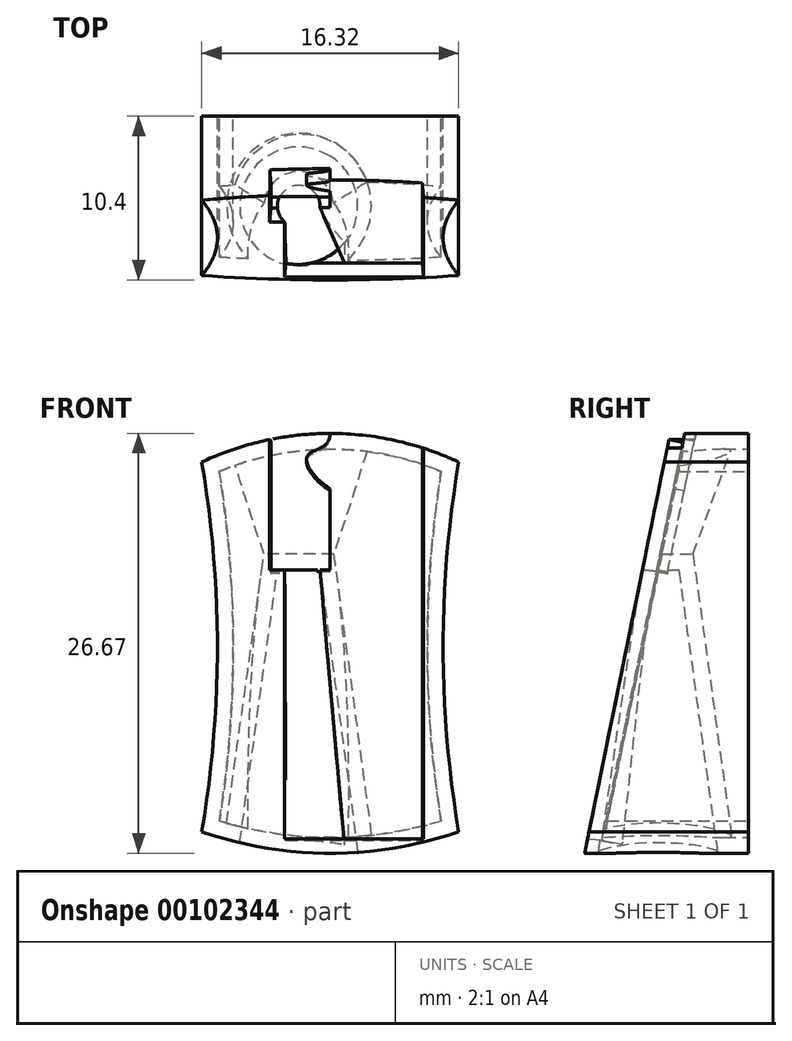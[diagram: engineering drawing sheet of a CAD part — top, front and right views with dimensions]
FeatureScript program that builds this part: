
annotation { "Feature Type Name" : "Feature", "Feature Type Description" : "" }
export const myFeature = defineFeature(function(context is Context, id is Id, definition is map)
    precondition{}
    {
        {
            var Q0;
            Q0=qCreatedBy(makeId("Front.planeOp"),FACE);
            var sketch = newSketch(context, id + "F0", { "sketchPlane" : qUnion([Q0])});
            skLineSegment(sketch, "E0", {"start": v(0, 26.67) * mm, "end": v(52.61, 26.67) * mm, "construction": true});
            skLineSegment(sketch, "E1", {"start": v(40.02, 26.67) * mm, "end": v(40.02, 0) * mm, "construction": true});
            skLineSegment(sketch, "E2", {"start": v(40.02, 13.34) * mm, "end": v(-78.87, 13.33) * mm, "construction": true});
            skLineSegment(sketch, "E3", {"start": v(0, 26.67) * mm, "end": v(0, 0) * mm});
            skPoint(sketch, "E4", {"position": v(-8.16, 1.37) * mm});
            skPoint(sketch, "E5", {"position": v(-8.16, 24.85) * mm});
            skArc(sketch, "E6.trimOffspring", {"start": v(-8.16, 1.37) * mm, "mid": v(-7.17, 13.1) * mm, "end": v(-8.16, 24.85) * mm});
            skArc(sketch, "E7.MirrorCS", {"start": v(8.16, 1.37) * mm, "mid": v(7.17, 13.1) * mm, "end": v(8.16, 24.85) * mm});
            skArc(sketch, "E8.trimOffspring", {"start": v(-8.16, 1.37) * mm, "mid": v(0, 0) * mm, "end": v(8.16, 1.37) * mm});
            skArc(sketch, "E9.trimOffspring", {"start": v(8.16, 24.85) * mm, "mid": v(0, 26.67) * mm, "end": v(-8.16, 24.85) * mm});
            skSolve(sketch);
        }
        {
            var Q0;
            Q0 = qSketchRegion(id + "F0", true);
            extrude(context, id + "F1", {"entities" : qUnion([Q0]), "endBound" : BoundingType.SYMMETRIC, "depth" : 11.45 * mm});
        }
        {
            var Q0;
            Q0=qCreatedBy(makeId("Right.planeOp"),FACE);
            cPlane(context, id + "F2", {"entities" : qUnion([Q0]), "cplaneType" : CPlaneType.OFFSET, "offset" : 2 * mm, "oppositeDirection" : true, "width" : 150 * mm, "height" : 150 * mm});
        }
        {
            var Q0;
            Q0=qCreatedBy(makeId("Top.planeOp"),FACE);
            cPlane(context, id + "F3", {"entities" : qUnion([Q0]), "cplaneType" : CPlaneType.OFFSET, "offset" : 18 * mm, "width" : 150 * mm, "height" : 150 * mm});
        }
        {
            var Q0;
            Q0=qCreatedBy(id+"F3.planeOp",FACE);
            var sketch = newSketch(context, id + "F4", { "sketchPlane" : qUnion([Q0])});
            skCircle(sketch, "E10", {"center": v(-2, 0) * mm, "radius": 1.34 * mm});
            skSolve(sketch);
        }
        {
            var Q0;
            Q0=qCreatedBy(makeId("Top.planeOp"),FACE);
            var sketch = newSketch(context, id + "F5", { "sketchPlane" : qUnion([Q0])});
            skCircle(sketch, "E11", {"center": v(-2.04, 0) * mm, "radius": 3.8 * mm});
            skSolve(sketch);
        }
        {
            var Q0;
            Q0=qCreatedBy(id+"F2.planeOp",FACE);
            var sketch = newSketch(context, id + "F6", { "sketchPlane" : qUnion([Q0])});
            skLineSegment(sketch, "E12", {"start": v(-7.25, -12.65) * mm, "end": v(3, 37.68) * mm});
            skLineSegment(sketch, "E13", {"start": v(-5.4, -3.63) * mm, "end": v(8.94, -3.63) * mm});
            skLineSegment(sketch, "E14", {"start": v(8.94, -3.63) * mm, "end": v(8.94, 28.25) * mm});
            skLineSegment(sketch, "E15", {"start": v(8.94, 28.25) * mm, "end": v(-12.13, 28.25) * mm});
            skLineSegment(sketch, "E16", {"start": v(-12.13, 28.25) * mm, "end": v(-12.13, -3.63) * mm});
            skLineSegment(sketch, "E17", {"start": v(-12.13, -3.63) * mm, "end": v(-5.4, -3.63) * mm});
            skSolve(sketch);
        }
        {
            var Q0;
            {var subQ4=sQuery(id+"F6.wireOp",EDGE,"E16");Q0=makeQuery(id+"F6.imprint","IMPRINT",FACE,{"disambiguationData":[TD([[makeQuery(id+"F6.imprint","IMPRINT",EDGE,{"derivedFrom":subQ4}),1.0]])]});}
            extrude(context, id + "F7", {"entities" : qUnion([Q0]), "operationType" : NewBodyOperationType.REMOVE, "endBound" : BoundingType.SYMMETRIC, "oppositeDirection" : true, "depth" : 25 * mm});
        }
        {
            var Q1;
            Q1=makeQuery(id+"F5.imprint","IMPRINT",FACE,{"disambiguationData":[TD([[makeQuery(id+"F5.imprint","IMPRINT",EDGE,{"derivedFrom":sQuery(id+"F5.wireOp",EDGE,"E11")}),1.0]])]});
            var Q2;
            Q2=makeQuery(id+"F4.imprint","IMPRINT",FACE,{"disambiguationData":[TD([[makeQuery(id+"F4.imprint","IMPRINT",EDGE,{"derivedFrom":sQuery(id+"F4.wireOp",EDGE,"E10")}),1.0]])]});
            loft(context, id + "F8", {"operationType" : NewBodyOperationType.REMOVE, "sheetProfilesArray" : [{ "sheetProfileEntities" : qUnion([Q1]) }, { "sheetProfileEntities" : qUnion([Q2]) }]});
        }
        {
            var Q0;
            Q0=makeQuery(id+"F7.boolean.opBoolean","COPY",FACE,{"derivedFrom":makeQuery(id+"F7.opExtrude","SWEPT_FACE",FACE,{"disambiguationData":[OSD([sQuery(id+"F6.wireOp",EDGE,"E12")])]})});
            var sketch = newSketch(context, id + "F9", { "sketchPlane" : qUnion([Q0])});
            skLineSegment(sketch, "E18", {"start": v(-2.9, 17.44) * mm, "end": v(-2.9, 0) * mm});
            skLineSegment(sketch, "E19", {"start": v(5.92, 25.33) * mm, "end": v(5.92, 0) * mm});
            skLineSegment(sketch, "E20", {"start": v(-2.9, 17.44) * mm, "end": v(-3.85, 17.44) * mm});
            skPoint(sketch, "E20.endSnap0", {"position": v(-2, 17.44) * mm});
            skLineSegment(sketch, "E21", {"start": v(-3.85, 17.44) * mm, "end": v(-3.85, 25.89) * mm});
            skLineSegment(sketch, "E22", {"start": v(-2.9, 0) * mm, "end": v(5.92, 0) * mm});
            skLineSegment(sketch, "E23", {"start": v(5.92, 25.33) * mm, "end": v(5.92, 28.98) * mm});
            skLineSegment(sketch, "E24", {"start": v(5.92, 28.98) * mm, "end": v(-4.7, 30.13) * mm});
            skLineSegment(sketch, "E25", {"start": v(-4.7, 30.13) * mm, "end": v(-3.85, 25.89) * mm});
            skSolve(sketch);
        }
        {
            var Q0;
            Q0=makeQuery(id+"F1.opExtrude","CAP_FACE",FACE,{"disambiguationData":[OSD([sQuery(id+"F0.wireOp",EDGE,"E6.trimOffspring"),sQuery(id+"F0.wireOp",EDGE,"E7.MirrorCS"),sQuery(id+"F0.wireOp",EDGE,"E8.trimOffspring"),sQuery(id+"F0.wireOp",EDGE,"E9.trimOffspring")])],"isStart":true});
            shell(context, id + "F10", {"entities" : qUnion([Q0]), "thickness" : 1 * mm});
        }
        {
            var Q0;
            Q0=makeQuery(id+"F10.opShell","OFFSET_FACE",FACE,{"disambiguationData":[OSD([makeQuery(id+"F4.imprint","IMPRINT",FACE,{"disambiguationData":[TD([[makeQuery(id+"F4.imprint","IMPRINT",EDGE,{"derivedFrom":sQuery(id+"F4.wireOp",EDGE,"E10")}),1.0]])]})])]});
            var sketch = newSketch(context, id + "F11", { "sketchPlane" : qUnion([Q0])});
            skLineSegment(sketch, "E26", {"start": v(0.2, 0.22) * mm, "end": v(-4.2, 0.22) * mm});
            skArc(sketch, "E27", {"start": v(0.2, 0.22) * mm, "mid": v(-2, 2.21) * mm, "end": v(-4.2, 0.22) * mm});
            skPoint(sketch, "E27.centerSnap0", {"position": v(-2, 0.22) * mm});
            skSolve(sketch);
        }
        {
            var Q0;
            Q0 = qSketchRegion(id + "F11", true);
            extrude(context, id + "F12", {"entities" : qUnion([Q0]), "operationType" : NewBodyOperationType.ADD, "endBound" : BoundingType.UP_TO_NEXT, "depth" : 5.68 * mm, "hasDraft" : true, "draftAngle" : 20 * degree});
        }
        {
            var Q0;
            Q0 = qSketchRegion(id + "F9", true);
            extrude(context, id + "F13", {"entities" : qUnion([Q0]), "operationType" : NewBodyOperationType.REMOVE, "oppositeDirection" : true, "depth" : 0.9 * mm, "hasDraft" : true, "draftAngle" : 5 * degree, "draftPullDirection" : true});
        }
        {
            var Q0;
            Q0=makeQuery(id+"F13.boolean.opBoolean","COPY",FACE,{"derivedFrom":makeQuery(id+"F13.opExtrude","CAP_FACE",FACE,{"disambiguationData":[OSD([sQuery(id+"F9.wireOp",EDGE,"E18"),sQuery(id+"F9.wireOp",EDGE,"E19"),sQuery(id+"F9.wireOp",EDGE,"E20"),sQuery(id+"F9.wireOp",EDGE,"E21"),sQuery(id+"F9.wireOp",EDGE,"E22"),sQuery(id+"F9.wireOp",EDGE,"44KTf25l-rCnn-U4tM-G2lu-nbjFAGZRS2s2")])],"isStart":false})});
            var sketch = newSketch(context, id + "F14", { "sketchPlane" : qUnion([Q0])});
            skLineSegment(sketch, "E28", {"start": v(0.9, 0.08) * mm, "end": v(-1.18, 0.08) * mm});
            skLineSegment(sketch, "E29", {"start": v(-1.18, 0.08) * mm, "end": v(-0.42, 14.92) * mm});
            skLineSegment(sketch, "E30", {"start": v(-0.42, 14.92) * mm, "end": v(0.9, 0.08) * mm});
            skSolve(sketch);
        }
        {
            var Q0;
            Q0 = qSketchRegion(id + "F14", true);
            extrude(context, id + "F15", {"entities" : qUnion([Q0]), "operationType" : NewBodyOperationType.REMOVE, "oppositeDirection" : true, "depth" : 1.3 * mm});
        }
        {
            var Q0;
            Q0=makeQuery(id+"F13.boolean.opBoolean","COPY",FACE,{"derivedFrom":makeQuery(id+"F13.opExtrude","CAP_FACE",FACE,{"disambiguationData":[OSD([sQuery(id+"F9.wireOp",EDGE,"E18"),sQuery(id+"F9.wireOp",EDGE,"E19"),sQuery(id+"F9.wireOp",EDGE,"E20"),sQuery(id+"F9.wireOp",EDGE,"E21"),sQuery(id+"F9.wireOp",EDGE,"E22"),sQuery(id+"F9.wireOp",EDGE,"44KTf25l-rCnn-U4tM-G2lu-nbjFAGZRS2s2")])],"isStart":false})});
            var sketch = newSketch(context, id + "F16", { "sketchPlane" : qUnion([Q0])});
            skLineSegment(sketch, "E31", {"start": v(0, 17.62) * mm, "end": v(0, 22.88) * mm});
            skLineSegment(sketch, "E32", {"start": v(0, 17.62) * mm, "end": v(-3.78, 17.52) * mm});
            skFitSpline(sketch, "E33", {"points": [v(0, 22.88) * mm, v(-1.42, 25.06) * mm, v(0, 26.47) * mm], "startDerivative": vector(-5.77, 3.75) * mm, "endDerivative": vector(0, 6.53) * mm});
            skLineSegment(sketch, "E34", {"start": v(0, 26.47) * mm, "end": v(0, 28.71) * mm});
            skLineSegment(sketch, "E35", {"start": v(0, 28.71) * mm, "end": v(-3.9, 28.54) * mm});
            skLineSegment(sketch, "E36", {"start": v(-3.78, 17.52) * mm, "end": v(-3.81, 26.08) * mm});
            skLineSegment(sketch, "E37", {"start": v(-3.81, 26.08) * mm, "end": v(-3.9, 28.54) * mm});
            skSolve(sketch);
        }
        {
            var Q0;
            Q0 = qSketchRegion(id + "F16", true);
            extrude(context, id + "F17", {"entities" : qUnion([Q0]), "operationType" : NewBodyOperationType.REMOVE, "oppositeDirection" : true, "depth" : 0.7 * mm});
        }
    });
